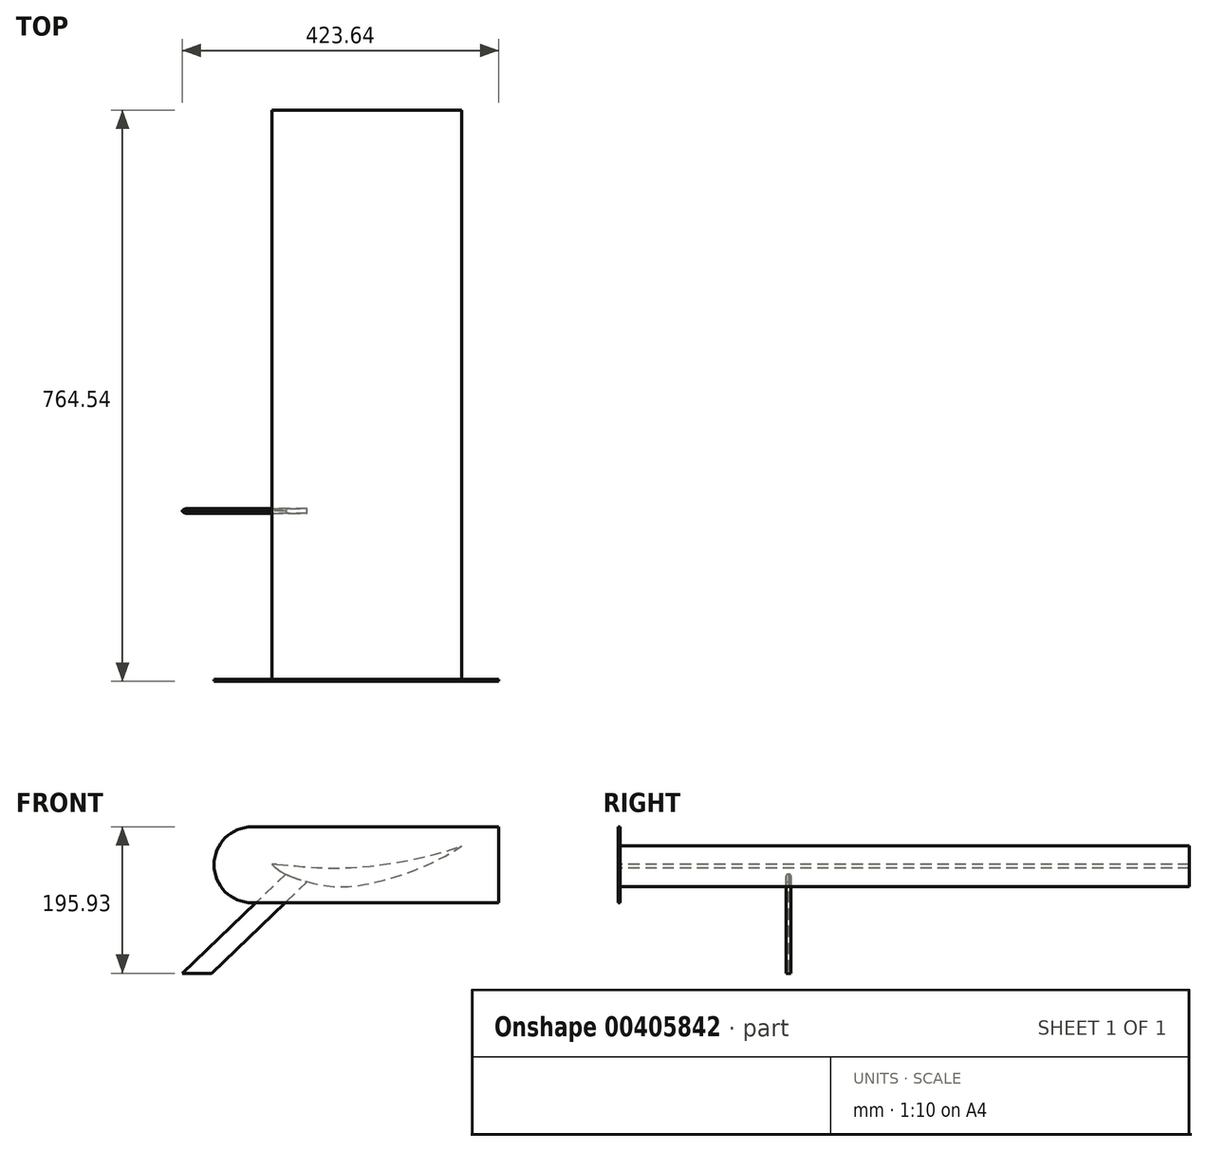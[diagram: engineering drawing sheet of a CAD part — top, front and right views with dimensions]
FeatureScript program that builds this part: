
annotation { "Feature Type Name" : "Feature", "Feature Type Description" : "" }
export const myFeature = defineFeature(function(context is Context, id is Id, definition is map)
    precondition{}
    {
        {
            var Q0;
            Q0=qCreatedBy(makeId("Front.planeOp"),FACE);
            var sketch = newSketch(context, id + "F0", { "sketchPlane" : qUnion([Q0])});
            skFitSpline(sketch, "E0", {"points": [v(-77.15, 7.84) * mm, v(28.7, 3.1) * mm, v(176.85, 32.33) * mm], "startDerivative": vector(173.85, -6.37) * mm, "endDerivative": vector(142.18, 61.99) * mm});
            skFitSpline(sketch, "E1", {"points": [v(-77.15, 7.84) * mm, v(-25.77, -16.9) * mm, v(45.1, -19.87) * mm, v(176.85, 32.33) * mm], "startDerivative": vector(113.43, -134.66) * mm, "endDerivative": vector(238.1, 171.84) * mm});
            skArc(sketch, "E2.filletArc", {"start": v(-70.48, 7.5) * mm, "mid": v(-73, 5.9) * mm, "end": v(-72.26, 3.02) * mm});
            skSolve(sketch);
        }
        {
            var Q0;
            Q0=makeQuery(id+"F0.imprint","IMPRINT",FACE,{"disambiguationData":[TD([[makeQuery(id+"F0.imprint","IMPRINT",EDGE,{"derivedFrom":sQuery(id+"F0.wireOp",EDGE,"E0")}),-1.0]])]});
            extrude(context, id + "F1", {"entities" : qUnion([Q0]), "endBound" : BoundingType.SYMMETRIC, "depth" : 762 * mm});
        }
        {
            var Q0;
            Q0=qCreatedBy(makeId("Front.planeOp"),FACE);
            cPlane(context, id + "F2", {"entities" : qUnion([Q0]), "cplaneType" : CPlaneType.OFFSET, "offset" : 152.4 * mm, "width" : 152.4 * mm, "height" : 152.4 * mm});
        }
        {
            var Q0;
            Q0=qCreatedBy(id+"F2.planeOp",FACE);
            var sketch = newSketch(context, id + "F3", { "sketchPlane" : qUnion([Q0])});
            skLineSegment(sketch, "E3", {"start": v(-18.48, -5.01) * mm, "end": v(-157.6, -138.27) * mm});
            skLineSegment(sketch, "E4", {"start": v(-157.6, -138.27) * mm, "end": v(-197.68, -138.27) * mm});
            skLineSegment(sketch, "E5", {"start": v(-197.68, -138.27) * mm, "end": v(-57.06, -3.58) * mm});
            skLineSegment(sketch, "E6", {"start": v(-57.06, -3.58) * mm, "end": v(-18.48, -5.01) * mm});
            skSolve(sketch);
        }
        {
            var Q0;
            Q0 = qSketchRegion(id + "F3", true);
            extrude(context, id + "F4", {"entities" : qUnion([Q0]), "operationType" : NewBodyOperationType.ADD, "depth" : 6.35 * mm});
        }
        {
            var Q0;
            Q0=makeQuery(id+"F1.opExtrude","CAP_FACE",FACE,{"disambiguationData":[OSD([sQuery(id+"F0.wireOp",EDGE,"E0"),sQuery(id+"F0.wireOp",EDGE,"E1"),sQuery(id+"F0.wireOp",EDGE,"E2.filletArc")])],"isStart":false});
            var sketch = newSketch(context, id + "F5", { "sketchPlane" : qUnion([Q0])});
            skLineSegment(sketch, "E7.bottom", {"start": v(-103.7, 57.66) * mm, "end": v(226.5, 57.66) * mm});
            skLineSegment(sketch, "E7.top", {"start": v(-103.7, -43.94) * mm, "end": v(226.5, -43.94) * mm});
            skLineSegment(sketch, "E7.left", {"start": v(-154.5, 6.86) * mm, "end": v(-154.5, 6.86) * mm});
            skLineSegment(sketch, "E7.right", {"start": v(226.5, 57.66) * mm, "end": v(226.5, -43.94) * mm});
            skPoint(sketch, "E8.visualSharp", {"position": v(-154.5, 57.66) * mm});
            skArc(sketch, "E8.filletArc", {"start": v(-103.7, 57.66) * mm, "mid": v(-139.63, 42.78) * mm, "end": v(-154.5, 6.86) * mm});
            skPoint(sketch, "E9.visualSharp", {"position": v(-154.5, -43.94) * mm});
            skArc(sketch, "E9.filletArc", {"start": v(-154.5, 6.86) * mm, "mid": v(-139.63, -29.06) * mm, "end": v(-103.7, -43.94) * mm});
            skSolve(sketch);
        }
        {
            var Q0;
            Q0 = qSketchRegion(id + "F5", true);
            extrude(context, id + "F6", {"entities" : qUnion([Q0]), "depth" : 2.54 * mm});
        }
        {
            var Q0;
            Q0=makeQuery(id+"FV90bI2RXGFGQP7_1.1.F4.opExtrude","CAP_EDGE",EDGE,{"disambiguationData":[OSD([sQuery(id+"F3.wireOp",EDGE,"E5")])],"isStart":false});
            var Q1;
            Q1=makeQuery(id+"FV90bI2RXGFGQP7_1.1.F4.opExtrude","CAP_EDGE",EDGE,{"disambiguationData":[OSD([sQuery(id+"F3.wireOp",EDGE,"E5")])],"isStart":true});
            var Q2;
            Q2=makeQuery(id+"F4.opExtrude","CAP_EDGE",EDGE,{"disambiguationData":[OSD([sQuery(id+"F3.wireOp",EDGE,"E5")])],"isStart":true});
            var Q3;
            Q3=makeQuery(id+"F4.opExtrude","CAP_EDGE",EDGE,{"disambiguationData":[OSD([sQuery(id+"F3.wireOp",EDGE,"E5")])],"isStart":false});
            fillet(context, id + "F7", {"entities" : qUnion([Q0, Q1, Q2, Q3]), "radius" : 5.08 * mm, "tangentPropagation" : true, "allowEdgeOverflow" : false});
        }
    });
